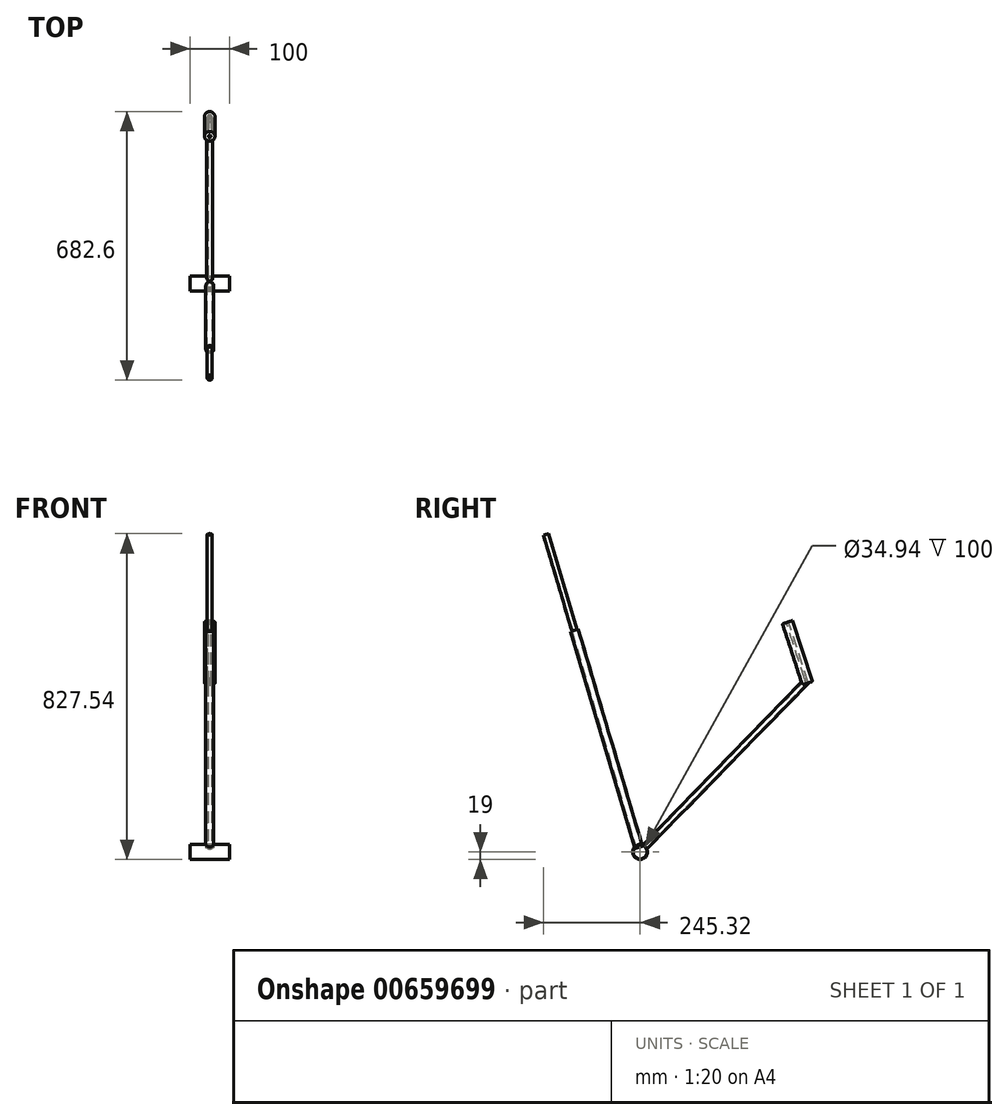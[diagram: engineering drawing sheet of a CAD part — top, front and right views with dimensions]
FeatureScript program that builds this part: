
annotation { "Feature Type Name" : "Feature", "Feature Type Description" : "" }
export const myFeature = defineFeature(function(context is Context, id is Id, definition is map)
    precondition{}
    {
        {
            var Q0;
            Q0=qCreatedBy(makeId("Right.planeOp"),FACE);
            var sketch = newSketch(context, id + "F0", { "sketchPlane" : qUnion([Q0])});
            skCircle(sketch, "E0", {"center": v(0, 0) * mm, "radius": 19.05 * mm, "construction": true});
            skLineSegment(sketch, "E1", {"start": v(0, 0) * mm, "end": v(-147.69, 498.59) * mm, "construction": true});
            skLineSegment(sketch, "E2", {"start": v(-435, 75) * mm, "end": v(580, 75) * mm, "construction": true});
            skLineSegment(sketch, "E3", {"start": v(0, 0) * mm, "end": v(0, 582) * mm, "construction": true});
            skLineSegment(sketch, "E4", {"start": v(535, 75) * mm, "end": v(384.92, 536.9) * mm, "construction": true});
            skCircle(sketch, "E5", {"center": v(-435, 75) * mm, "radius": 350 * mm, "construction": true});
            skCircle(sketch, "E6", {"center": v(580, 75) * mm, "radius": 350 * mm, "construction": true});
            skLineSegment(sketch, "E7", {"start": v(-192.59, 614.25) * mm, "end": v(354.41, 614.25) * mm, "construction": true});
            skLineSegment(sketch, "E8", {"start": v(0, 582) * mm, "end": v(375, 582) * mm, "construction": true});
            skLineSegment(sketch, "E9", {"start": v(375, 582) * mm, "end": v(424.44, 429.83) * mm});
            skLineSegment(sketch, "E10", {"start": v(-435, 75) * mm, "end": v(0, 0) * mm});
            skLineSegment(sketch, "E11", {"start": v(0, 0) * mm, "end": v(419.45, 430.61) * mm});
            skLineSegment(sketch, "E12", {"start": v(419.45, 430.61) * mm, "end": v(371.97, 576.74) * mm});
            skLineSegment(sketch, "E13", {"start": v(371.97, 576.74) * mm, "end": v(-147.69, 498.59) * mm});
            skLineSegment(sketch, "E14", {"start": v(-147.69, 498.59) * mm, "end": v(-435, 75) * mm});
            skCircle(sketch, "E15", {"center": v(0, 0) * mm, "radius": 19 * mm});
            skCircle(sketch, "E16", {"center": v(0, 0) * mm, "radius": 17.47 * mm});
            skSolve(sketch);
        }
        {
            var Q0;
            {var subQ0=sQuery(id+"F0.wireOp",EDGE,"E15");var subQ1=sQuery(id+"F0.wireOp",EDGE,"E10");var subQ2=makeQuery(id+"F0.imprint","INTERSECT",VERTEX,{"derivedFrom":[subQ1,subQ0]});Q0=makeQuery(id+"F0.imprint","IMPRINT",FACE,{"disambiguationData":[TD([[makeQuery(id+"F0.imprint","IMPRINT",EDGE,{"disambiguationData":[TD([[subQ2,-1.0]])],"derivedFrom":subQ1}),-1.0]])]});}
            var Q1;
            {var subQ0=sQuery(id+"F0.wireOp",EDGE,"E15");var subQ1=sQuery(id+"F0.wireOp",EDGE,"E10");var subQ2=makeQuery(id+"F0.imprint","INTERSECT",VERTEX,{"derivedFrom":[subQ1,subQ0]});Q1=makeQuery(id+"F0.imprint","IMPRINT",FACE,{"disambiguationData":[TD([[makeQuery(id+"F0.imprint","IMPRINT",EDGE,{"disambiguationData":[TD([[subQ2,-1.0]])],"derivedFrom":subQ1}),1.0]])]});}
            extrude(context, id + "F1", {"entities" : qUnion([Q0, Q1]), "oppositeDirection" : true, "depth" : 50 * mm, "offsetDistance" : 25 * mm, "hasSecondDirection" : true, "secondDirectionOppositeDirection" : false, "secondDirectionDepth" : 50 * mm});
        }
        {
            var Q0;
            Q0=qCreatedBy(makeId("Right.planeOp"),FACE);
            var sketch = newSketch(context, id + "F2", { "sketchPlane" : qUnion([Q0])});
            skLineSegment(sketch, "E17", {"start": v(6.1, 14.63) * mm, "end": v(-157.21, 565.95) * mm});
            skLineSegment(sketch, "E18.0", {"start": v(3.22, 13.78) * mm, "end": v(-160.09, 565.1) * mm});
            skLineSegment(sketch, "E19", {"start": v(-157.21, 565.95) * mm, "end": v(-160.09, 565.1) * mm});
            skLineSegment(sketch, "E20", {"start": v(6.1, 14.63) * mm, "end": v(3.22, 13.78) * mm});
            skSolve(sketch);
        }
        {
            var Q0;
            Q0 = qSketchRegion(id + "F2", true);
            var Q1;
            Q1=sQuery(id+"F0.wireOp",EDGE,"E1");
            revolve(context, id + "F3", {"operationType" : NewBodyOperationType.ADD, "entities" : qUnion([Q0]), "axis" : qUnion([Q1]), "revolveType" : RevolveType.FULL});
        }
        {
            var Q0;
            Q0=makeQuery(id+"F3.opRevolve","SWEPT_FACE",FACE,{"disambiguationData":[OSD([sQuery(id+"F2.wireOp",EDGE,"E19")])]});
            var sketch = newSketch(context, id + "F4", { "sketchPlane" : qUnion([Q0])});
            skCircle(sketch, "E21", {"center": v(0, 0) * mm, "radius": 6.65 * mm});
            skCircle(sketch, "E22", {"center": v(0, 0) * mm, "radius": 4.93 * mm});
            skSolve(sketch);
        }
        {
            var Q0;
            Q0 = qSketchRegion(id + "F4", true);
            extrude(context, id + "F5", {"entities" : qUnion([Q0]), "depth" : 254 * mm, "offsetDistance" : 25 * mm});
        }
        {
            var Q0;
            Q0=qCreatedBy(makeId("Right.planeOp"),FACE);
            var sketch = newSketch(context, id + "F6", { "sketchPlane" : qUnion([Q0])});
            skLineSegment(sketch, "E23", {"start": v(15.5, 9.18) * mm, "end": v(427.17, 431.79) * mm});
            skLineSegment(sketch, "E24", {"start": v(429.12, 429.88) * mm, "end": v(17.47, 7.27) * mm});
            skLineSegment(sketch, "E25", {"start": v(15.5, 9.18) * mm, "end": v(17.47, 7.27) * mm});
            skLineSegment(sketch, "E26", {"start": v(427.17, 431.79) * mm, "end": v(429.12, 429.88) * mm});
            skSolve(sketch);
        }
        {
            var Q0;
            Q0 = qSketchRegion(id + "F6", true);
            var Q1;
            Q1=sQuery(id+"F0.wireOp",EDGE,"E11");
            revolve(context, id + "F7", {"operationType" : NewBodyOperationType.ADD, "entities" : qUnion([Q0]), "axis" : qUnion([Q1]), "revolveType" : RevolveType.FULL});
        }
        {
            var Q0;
            Q0=qCreatedBy(makeId("Right.planeOp"),FACE);
            var sketch = newSketch(context, id + "F8", { "sketchPlane" : qUnion([Q0])});
            skLineSegment(sketch, "E27", {"start": v(437.28, 432.9) * mm, "end": v(386.96, 587.78) * mm});
            skLineSegment(sketch, "E28", {"start": v(386.96, 587.78) * mm, "end": v(377.25, 584.62) * mm});
            skLineSegment(sketch, "E29", {"start": v(377.25, 584.62) * mm, "end": v(427.57, 429.75) * mm});
            skLineSegment(sketch, "E30", {"start": v(427.57, 429.75) * mm, "end": v(437.28, 432.9) * mm});
            skSolve(sketch);
        }
        {
            var Q0;
            Q0 = qSketchRegion(id + "F8", true);
            var Q1;
            Q1=sQuery(id+"F0.wireOp",EDGE,"E9");
            revolve(context, id + "F9", {"operationType" : NewBodyOperationType.ADD, "entities" : qUnion([Q0]), "axis" : qUnion([Q1]), "revolveType" : RevolveType.FULL});
        }
    });
